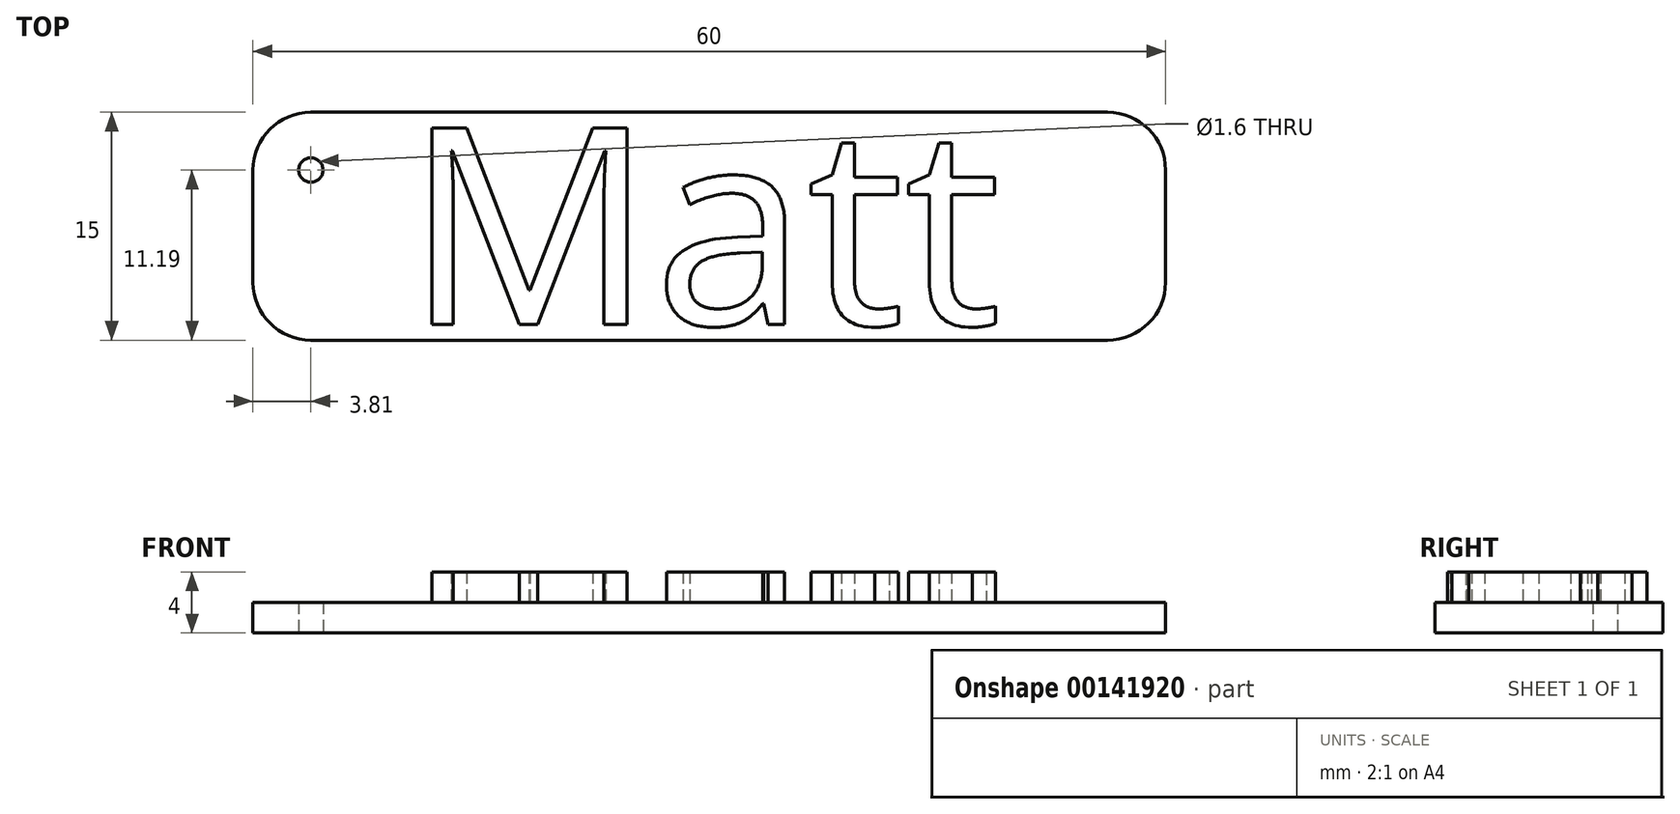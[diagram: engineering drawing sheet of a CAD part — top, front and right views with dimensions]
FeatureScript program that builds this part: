
annotation { "Feature Type Name" : "Feature", "Feature Type Description" : "" }
export const myFeature = defineFeature(function(context is Context, id is Id, definition is map)
    precondition{}
    {
        {
            var Q0;
            Q0=qCreatedBy(makeId("Top.planeOp"),FACE);
            var sketch = newSketch(context, id + "F0", { "sketchPlane" : qUnion([Q0])});
            skLineSegment(sketch, "E0.bottom", {"start": v(26.19, 7.5) * mm, "end": v(-26.19, 7.5) * mm});
            skLineSegment(sketch, "E0.top", {"start": v(26.19, -7.5) * mm, "end": v(-26.19, -7.5) * mm});
            skLineSegment(sketch, "E0.left", {"start": v(30, 3.7) * mm, "end": v(30, -3.7) * mm});
            skLineSegment(sketch, "E0.right", {"start": v(-30, 3.7) * mm, "end": v(-30, -3.7) * mm});
            skPoint(sketch, "E0.middle", {"position": v(0, 0) * mm});
            skText(sketch, "E1", { "text": "Matt", "fontName": "OpenSans-Regular.ttf"});
            skPoint(sketch, "E2.visualSharp", {"position": v(-30, -7.5) * mm});
            skArc(sketch, "E2.filletArc", {"start": v(-30, -3.7) * mm, "mid": v(-28.88, -6.38) * mm, "end": v(-26.19, -7.5) * mm});
            skPoint(sketch, "E3.visualSharp", {"position": v(-30, 7.5) * mm});
            skArc(sketch, "E3.filletArc", {"start": v(-26.19, 7.5) * mm, "mid": v(-28.88, 6.38) * mm, "end": v(-30, 3.7) * mm});
            skPoint(sketch, "E4.visualSharp", {"position": v(30, -7.5) * mm});
            skArc(sketch, "E4.filletArc", {"start": v(26.19, -7.5) * mm, "mid": v(28.88, -6.38) * mm, "end": v(30, -3.7) * mm});
            skPoint(sketch, "E5.visualSharp", {"position": v(30, 7.5) * mm});
            skArc(sketch, "E5.filletArc", {"start": v(30, 3.7) * mm, "mid": v(28.88, 6.38) * mm, "end": v(26.19, 7.5) * mm});
            skCircle(sketch, "E6", {"center": v(-26.19, 3.7) * mm, "radius": 0.8 * mm});
            const initialGuessF0  = {"E1": [-0.02, -0.00648, 1, 0, 0.01304]};
            skSetInitialGuess(sketch, initialGuessF0);
            skSolve(sketch);
        }
        {
            var Q0;
            Q0=makeQuery(id+"F0.imprint","IMPRINT",FACE,{"disambiguationData":[TD([[makeQuery(id+"F0.imprint","IMPRINT",EDGE,{"derivedFrom":sQuery(id+"F0.wireOp",EDGE,"E0.bottom")}),1.0]])]});
            extrude(context, id + "F1", {"entities" : qUnion([Q0]), "depth" : 2 * mm});
        }
        {
            var Q0;
            Q0=makeQuery(id+"F0.imprint","IMPRINT",FACE,{"disambiguationData":[TD([[makeQuery(id+"F0.imprint","IMPRINT",EDGE,{"derivedFrom":sQuery(id+"F0.wireOp",EDGE,"E1.sketch_text.stroke-18")}),-1.0]])]});
            extrude(context, id + "F2", {"entities" : qUnion([Q0]), "operationType" : NewBodyOperationType.ADD, "depth" : 4 * mm});
        }
        {
            var Q0;
            Q0=makeQuery(id+"F0.imprint","IMPRINT",FACE,{"disambiguationData":[TD([[makeQuery(id+"F0.imprint","IMPRINT",EDGE,{"derivedFrom":sQuery(id+"F0.wireOp",EDGE,"E1.sketch_text.stroke-0")}),-1.0]])]});
            extrude(context, id + "F3", {"entities" : qUnion([Q0]), "operationType" : NewBodyOperationType.ADD, "depth" : 4 * mm});
        }
        {
            var Q0;
            Q0=makeQuery(id+"F0.imprint","IMPRINT",FACE,{"disambiguationData":[TD([[makeQuery(id+"F0.imprint","IMPRINT",EDGE,{"derivedFrom":sQuery(id+"F0.wireOp",EDGE,"E1.sketch_text.stroke-37")}),1.0]])]});
            extrude(context, id + "F4", {"entities" : qUnion([Q0]), "operationType" : NewBodyOperationType.ADD, "depth" : 2 * mm});
        }
        {
            var Q0;
            Q0=makeQuery(id+"F0.imprint","IMPRINT",FACE,{"disambiguationData":[TD([[makeQuery(id+"F0.imprint","IMPRINT",EDGE,{"derivedFrom":sQuery(id+"F0.wireOp",EDGE,"E1.sketch_text.stroke-45")}),-1.0]])]});
            var Q1;
            Q1=makeQuery(id+"F0.imprint","IMPRINT",FACE,{"disambiguationData":[TD([[makeQuery(id+"F0.imprint","IMPRINT",EDGE,{"derivedFrom":sQuery(id+"F0.wireOp",EDGE,"E1.sketch_text.stroke-64")}),-1.0]])]});
            extrude(context, id + "F5", {"entities" : qUnion([Q0, Q1]), "operationType" : NewBodyOperationType.ADD, "depth" : 4 * mm});
        }
        {
            var Q0;
            Q0=makeQuery(id+"F3.opExtrude","CAP_FACE",FACE,{"disambiguationData":[OSD([sQuery(id+"F0.wireOp",EDGE,"E1.sketch_text.stroke-0"),sQuery(id+"F0.wireOp",EDGE,"E1.sketch_text.stroke-1"),sQuery(id+"F0.wireOp",EDGE,"E1.sketch_text.stroke-2"),sQuery(id+"F0.wireOp",EDGE,"E1.sketch_text.stroke-3"),sQuery(id+"F0.wireOp",EDGE,"E1.sketch_text.stroke-4"),sQuery(id+"F0.wireOp",EDGE,"E1.sketch_text.stroke-5"),sQuery(id+"F0.wireOp",EDGE,"E1.sketch_text.stroke-6"),sQuery(id+"F0.wireOp",EDGE,"E1.sketch_text.stroke-7"),sQuery(id+"F0.wireOp",EDGE,"E1.sketch_text.stroke-8"),sQuery(id+"F0.wireOp",EDGE,"E1.sketch_text.stroke-9"),sQuery(id+"F0.wireOp",EDGE,"E1.sketch_text.stroke-10"),sQuery(id+"F0.wireOp",EDGE,"E1.sketch_text.stroke-11"),sQuery(id+"F0.wireOp",EDGE,"E1.sketch_text.stroke-12"),sQuery(id+"F0.wireOp",EDGE,"E1.sketch_text.stroke-13"),sQuery(id+"F0.wireOp",EDGE,"E1.sketch_text.stroke-14"),sQuery(id+"F0.wireOp",EDGE,"E1.sketch_text.stroke-15"),sQuery(id+"F0.wireOp",EDGE,"E1.sketch_text.stroke-16"),sQuery(id+"F0.wireOp",EDGE,"E1.sketch_text.stroke-17")])],"isStart":false});
            extrude(context, id + "F6", {"entities" : qUnion([Q0]), "operationType" : NewBodyOperationType.ADD, "oppositeDirection" : true, "depth" : 2.5 * mm});
        }
    });
